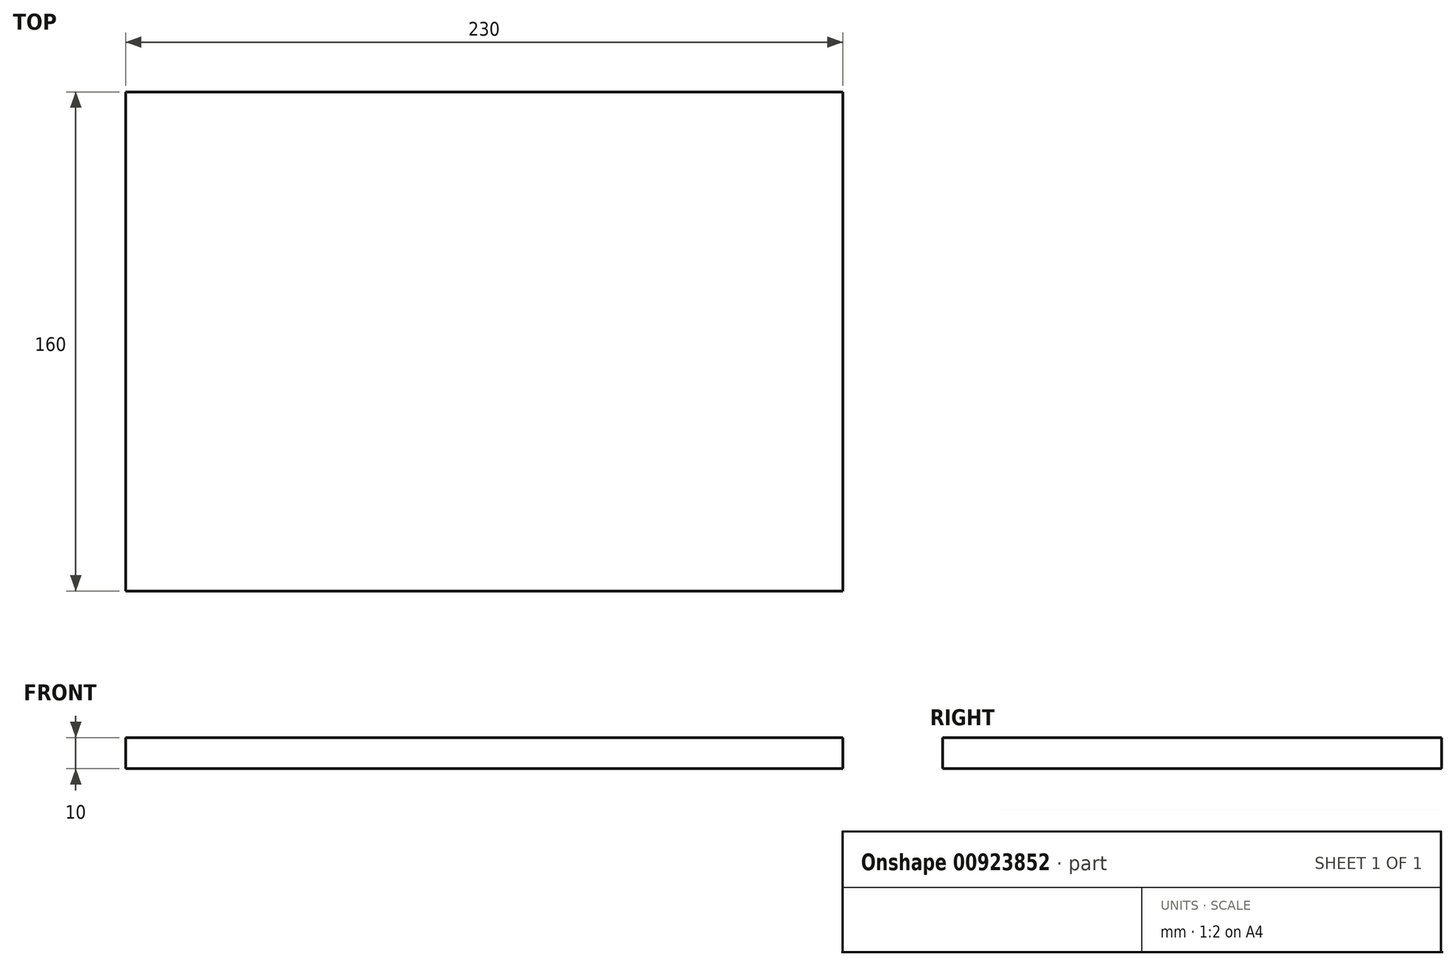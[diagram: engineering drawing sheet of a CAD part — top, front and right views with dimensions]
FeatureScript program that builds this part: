
annotation { "Feature Type Name" : "Feature", "Feature Type Description" : "" }
export const myFeature = defineFeature(function(context is Context, id is Id, definition is map)
    precondition{}
    {
        {
            var Q0;
            Q0=qCreatedBy(makeId("Top.planeOp"),FACE);
            var sketch = newSketch(context, id + "F0", { "sketchPlane" : qUnion([Q0])});
            skPoint(sketch, "E0.middle", {"position": v(0, 0) * mm});
            skLineSegment(sketch, "E1.bottom", {"start": v(115, 80) * mm, "end": v(-115, 80) * mm});
            skLineSegment(sketch, "E1.top", {"start": v(115, -80) * mm, "end": v(-115, -80) * mm});
            skLineSegment(sketch, "E1.left", {"start": v(115, 80) * mm, "end": v(115, -80) * mm});
            skLineSegment(sketch, "E1.right", {"start": v(-115, 80) * mm, "end": v(-115, -80) * mm});
            skSolve(sketch);
        }
        {
            var Q0;
            Q0=makeQuery(id+"F0.imprint","IMPRINT",FACE,{"disambiguationData":[TD([[makeQuery(id+"F0.imprint","IMPRINT",EDGE,{"derivedFrom":sQuery(id+"F0.wireOp",EDGE,"E0.bottom")}),1.0]])]});
            var Q1;
            Q1=makeQuery(id+"F0.imprint","IMPRINT",FACE,{"disambiguationData":[TD([[makeQuery(id+"F0.imprint","IMPRINT",EDGE,{"derivedFrom":sQuery(id+"F0.wireOp",EDGE,"E1.bottom")}),1.0]])]});
            extrude(context, id + "F1", {"entities" : qUnion([Q0, Q1]), "depth" : 10 * mm, "offsetDistance" : 25 * mm});
        }
    });
